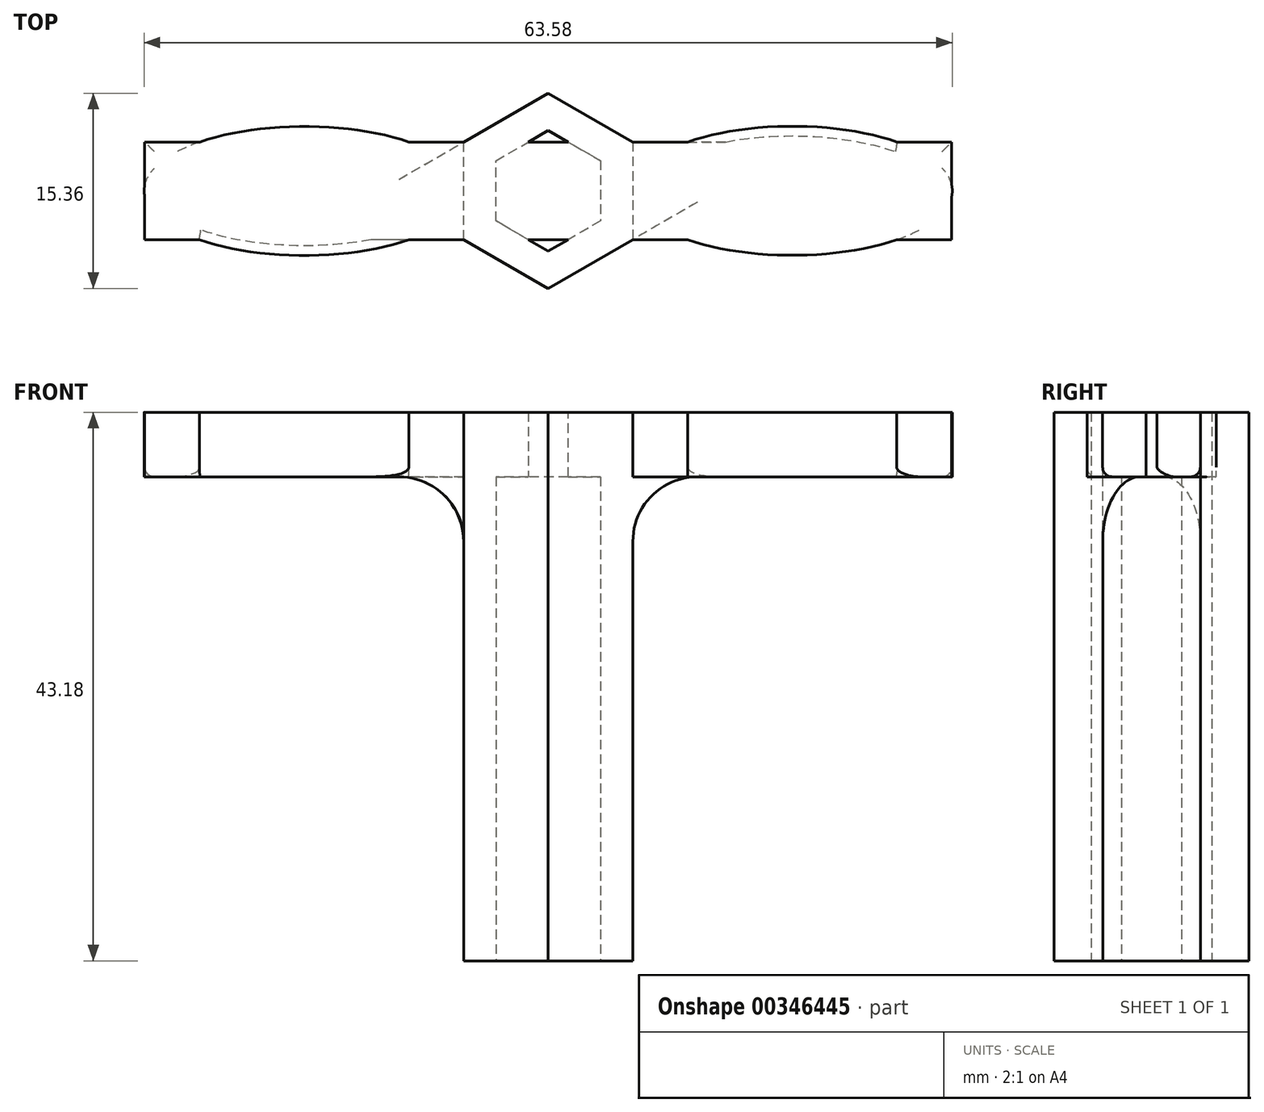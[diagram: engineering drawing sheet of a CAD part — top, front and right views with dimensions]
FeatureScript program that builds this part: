
annotation { "Feature Type Name" : "Feature", "Feature Type Description" : "" }
export const myFeature = defineFeature(function(context is Context, id is Id, definition is map)
    precondition{}
    {
        {
            var Q0;
            Q0=qCreatedBy(makeId("Top.planeOp"),FACE);
            var sketch = newSketch(context, id + "F0", { "sketchPlane" : qUnion([Q0])});
            skCircle(sketch, "E0.cCircle", {"center": v(0, 0) * mm, "radius": 4.11 * mm, "construction": true});
            skLineSegment(sketch, "E0.0", {"start": v(0, 4.75) * mm, "end": v(4.11, 2.38) * mm});
            skLineSegment(sketch, "E0.1", {"start": v(4.11, 2.38) * mm, "end": v(4.11, -2.37) * mm});
            skLineSegment(sketch, "E0.2", {"start": v(4.11, -2.37) * mm, "end": v(0, -4.75) * mm});
            skLineSegment(sketch, "E0.3", {"start": v(0, -4.75) * mm, "end": v(-4.11, -2.38) * mm});
            skLineSegment(sketch, "E0.4", {"start": v(-4.11, -2.38) * mm, "end": v(-4.11, 2.37) * mm});
            skLineSegment(sketch, "E0.5", {"start": v(-4.11, 2.37) * mm, "end": v(0, 4.75) * mm});
            skPoint(sketch, "E0.0.midPoint", {"position": v(2.06, 3.56) * mm});
            skCircle(sketch, "E1.cCircle", {"center": v(0, 0) * mm, "radius": 6.65 * mm, "construction": true});
            skLineSegment(sketch, "E1.0", {"start": v(0, 7.68) * mm, "end": v(6.65, 3.84) * mm});
            skLineSegment(sketch, "E1.1", {"start": v(6.65, 3.84) * mm, "end": v(6.65, -3.84) * mm});
            skLineSegment(sketch, "E1.2", {"start": v(6.65, -3.84) * mm, "end": v(0, -7.68) * mm});
            skLineSegment(sketch, "E1.3", {"start": v(0, -7.68) * mm, "end": v(-6.65, -3.84) * mm});
            skLineSegment(sketch, "E1.4", {"start": v(-6.65, -3.84) * mm, "end": v(-6.65, 3.84) * mm});
            skLineSegment(sketch, "E1.5", {"start": v(-6.65, 3.84) * mm, "end": v(0, 7.68) * mm});
            skPoint(sketch, "E1.0.midPoint", {"position": v(3.32, 5.76) * mm});
            skSolve(sketch);
        }
        {
            var Q0;
            Q0=qSketchRegion(id+"F0",true);
            extrude(context, id + "F1", {"entities" : qUnion([Q0]), "depth" : 43.18 * mm});
        }
        {
            var Q0;
            Q0=makeQuery(id+"F1.opExtrude","CAP_FACE",FACE,{"disambiguationData":[OSD([sQuery(id+"F0.wireOp",EDGE,"E0.0"),sQuery(id+"F0.wireOp",EDGE,"E0.1"),sQuery(id+"F0.wireOp",EDGE,"E0.2"),sQuery(id+"F0.wireOp",EDGE,"E0.3"),sQuery(id+"F0.wireOp",EDGE,"E0.4"),sQuery(id+"F0.wireOp",EDGE,"E0.5"),sQuery(id+"F0.wireOp",EDGE,"E1.0"),sQuery(id+"F0.wireOp",EDGE,"E1.1"),sQuery(id+"F0.wireOp",EDGE,"E1.2"),sQuery(id+"F0.wireOp",EDGE,"E1.3"),sQuery(id+"F0.wireOp",EDGE,"E1.4"),sQuery(id+"F0.wireOp",EDGE,"E1.5")])],"isStart":false});
            var sketch = newSketch(context, id + "F2", { "sketchPlane" : qUnion([Q0])});
            skLineSegment(sketch, "E2", {"start": v(0, 4.75) * mm, "end": v(0, -4.75) * mm});
            skLineSegment(sketch, "E3.bottom", {"start": v(31.75, 3.84) * mm, "end": v(-31.75, 3.84) * mm});
            skLineSegment(sketch, "E3.top", {"start": v(31.75, -3.84) * mm, "end": v(-31.75, -3.84) * mm});
            skLineSegment(sketch, "E3.left", {"start": v(31.75, 3.84) * mm, "end": v(31.75, -3.84) * mm});
            skLineSegment(sketch, "E3.right", {"start": v(-31.75, 3.84) * mm, "end": v(-31.75, -3.84) * mm});
            skPoint(sketch, "E3.middle", {"position": v(0, 0) * mm});
            skLineSegment(sketch, "E4", {"start": v(-6.65, 0) * mm, "end": v(-31.75, -0.01) * mm});
            skEllipse(sketch, "E5", {"center": v(-19.2, 0) * mm, "majorRadius": 12.6 * mm, "minorRadius": 5.08 * mm, "majorAxis": v(-1, 0)});
            skLineSegment(sketch, "E6", {"start": v(6.65, 0) * mm, "end": v(31.75, 0) * mm});
            skEllipse(sketch, "E7", {"center": v(19.2, 0) * mm, "majorRadius": 12.6 * mm, "minorRadius": 5.08 * mm, "majorAxis": v(1, 0)});
            skSolve(sketch);
        }
        {
            var Q0;
            Q0 = qSketchRegion(id + "F2", true);
            extrude(context, id + "F3", {"entities" : qUnion([Q0]), "operationType" : NewBodyOperationType.ADD, "oppositeDirection" : true, "depth" : 5.08 * mm});
        }
        {
            var Q0;
            {var subQ0=sQuery(id+"F2.wireOp",EDGE,"E5");var subQ1=sQuery(id+"F2.wireOp",EDGE,"E3.bottom");Q0=makeQuery(id+"F3.opExtrude","CAP_EDGE",EDGE,{"disambiguationData":[OSD([subQ0]),TDD([makeQuery(id+"F2.imprint","IMPRINT",EDGE,{"disambiguationData":[TD([[makeQuery(id+"F2.imprint","INTERSECT",VERTEX,{"disambiguationData":[OD(0.0)],"derivedFrom":[subQ1,subQ0]}),-1.0]])],"derivedFrom":subQ0})])],"isStart":false});}
            var Q1;
            {var subQ0=sQuery(id+"F2.wireOp",EDGE,"E3.bottom");Q1=makeQuery(id+"F3.opExtrude","CAP_EDGE",EDGE,{"disambiguationData":[OSD([subQ0]),TDD([makeQuery(id+"F2.imprint","IMPRINT",EDGE,{"disambiguationData":[TD([[makeQuery(id+"F2.imprint","INTERSECT",VERTEX,{"derivedFrom":[subQ0,sQuery(id+"F2.wireOp",EDGE,"E3.right")]}),1.0]])],"derivedFrom":subQ0})])],"isStart":false});}
            var Q2;
            {var subQ0=sQuery(id+"F2.wireOp",EDGE,"E3.top");Q2=makeQuery(id+"F3.opExtrude","CAP_EDGE",EDGE,{"disambiguationData":[OSD([subQ0]),TDD([makeQuery(id+"F2.imprint","IMPRINT",EDGE,{"disambiguationData":[TD([[makeQuery(id+"F2.imprint","INTERSECT",VERTEX,{"derivedFrom":[subQ0,sQuery(id+"F2.wireOp",EDGE,"E3.right")]}),1.0]])],"derivedFrom":subQ0})])],"isStart":false});}
            var Q3;
            {var subQ0=sQuery(id+"F2.wireOp",EDGE,"E5");var subQ1=sQuery(id+"F2.wireOp",EDGE,"E3.top");Q3=makeQuery(id+"F3.opExtrude","CAP_EDGE",EDGE,{"disambiguationData":[OSD([subQ0]),TDD([makeQuery(id+"F2.imprint","IMPRINT",EDGE,{"disambiguationData":[TD([[makeQuery(id+"F2.imprint","INTERSECT",VERTEX,{"disambiguationData":[OD(0.0)],"derivedFrom":[subQ1,subQ0]}),1.0]])],"derivedFrom":subQ0})])],"isStart":false});}
            var Q4;
            {var subQ0=sQuery(id+"F2.wireOp",EDGE,"E3.right");Q4=makeQuery(id+"F3.opExtrude","CAP_EDGE",EDGE,{"disambiguationData":[OSD([subQ0]),TDD([makeQuery(id+"F2.imprint","IMPRINT",EDGE,{"disambiguationData":[TD([[makeQuery(id+"F2.imprint","INTERSECT",VERTEX,{"derivedFrom":[sQuery(id+"F2.wireOp",EDGE,"E3.bottom"),subQ0]}),-1.0]])],"derivedFrom":subQ0})])],"isStart":false});}
            var Q5;
            {var subQ0=sQuery(id+"F2.wireOp",EDGE,"E3.left");Q5=makeQuery(id+"F3.opExtrude","CAP_EDGE",EDGE,{"disambiguationData":[OSD([subQ0]),TDD([makeQuery(id+"F2.imprint","IMPRINT",EDGE,{"disambiguationData":[TD([[makeQuery(id+"F2.imprint","INTERSECT",VERTEX,{"derivedFrom":[sQuery(id+"F2.wireOp",EDGE,"E3.bottom"),subQ0]}),-1.0]])],"derivedFrom":subQ0})])],"isStart":false});}
            var Q6;
            {var subQ0=sQuery(id+"F2.wireOp",EDGE,"E3.top");Q6=makeQuery(id+"F3.opExtrude","CAP_EDGE",EDGE,{"disambiguationData":[OSD([subQ0]),TDD([makeQuery(id+"F2.imprint","IMPRINT",EDGE,{"disambiguationData":[TD([[makeQuery(id+"F2.imprint","INTERSECT",VERTEX,{"derivedFrom":[subQ0,sQuery(id+"F2.wireOp",EDGE,"E3.left")]}),-1.0]])],"derivedFrom":subQ0})])],"isStart":false});}
            var Q7;
            {var subQ0=sQuery(id+"F2.wireOp",EDGE,"E7");var subQ1=sQuery(id+"F2.wireOp",EDGE,"E3.top");Q7=makeQuery(id+"F3.opExtrude","CAP_EDGE",EDGE,{"disambiguationData":[OSD([subQ0]),TDD([makeQuery(id+"F2.imprint","IMPRINT",EDGE,{"disambiguationData":[TD([[makeQuery(id+"F2.imprint","INTERSECT",VERTEX,{"disambiguationData":[OD(0.0)],"derivedFrom":[subQ1,subQ0]}),1.0]])],"derivedFrom":subQ0})])],"isStart":false});}
            var Q8;
            {var subQ0=sQuery(id+"F2.wireOp",EDGE,"E7");var subQ1=sQuery(id+"F2.wireOp",EDGE,"E3.bottom");Q8=makeQuery(id+"F3.opExtrude","CAP_EDGE",EDGE,{"disambiguationData":[OSD([subQ0]),TDD([makeQuery(id+"F2.imprint","IMPRINT",EDGE,{"disambiguationData":[TD([[makeQuery(id+"F2.imprint","INTERSECT",VERTEX,{"disambiguationData":[OD(0.0)],"derivedFrom":[subQ1,subQ0]}),-1.0]])],"derivedFrom":subQ0})])],"isStart":false});}
            var Q9;
            {var subQ0=sQuery(id+"F2.wireOp",EDGE,"E3.bottom");Q9=makeQuery(id+"F3.opExtrude","CAP_EDGE",EDGE,{"disambiguationData":[OSD([subQ0]),TDD([makeQuery(id+"F2.imprint","IMPRINT",EDGE,{"disambiguationData":[TD([[makeQuery(id+"F2.imprint","INTERSECT",VERTEX,{"derivedFrom":[subQ0,sQuery(id+"F2.wireOp",EDGE,"E3.left")]}),-1.0]])],"derivedFrom":subQ0})])],"isStart":false});}
            fillet(context, id + "F4", {"entities" : qUnion([Q0, Q1, Q2, Q3, Q4, Q5, Q6, Q7, Q8, Q9]), "radius" : 0.76 * mm, "tangentPropagation" : true, "allowEdgeOverflow" : false});
        }
        {
            var Q0;
            Q0=makeQuery(id+"F3.boolean.opBoolean","INTERSECT",EDGE,{"derivedFrom":[makeQuery(id+"F1.opExtrude","SWEPT_FACE",FACE,{"disambiguationData":[OSD([sQuery(id+"F0.wireOp",EDGE,"E1.1")])]}),makeQuery(id+"F3.opExtrude","CAP_FACE",FACE,{"disambiguationData":[OSD([sQuery(id+"F2.wireOp",EDGE,"E3.bottom"),sQuery(id+"F2.wireOp",EDGE,"E3.top"),sQuery(id+"F2.wireOp",EDGE,"E3.left"),sQuery(id+"F2.wireOp",EDGE,"E3.right"),sQuery(id+"F2.wireOp",EDGE,"E5"),sQuery(id+"F2.wireOp",EDGE,"E7")])],"isStart":false})]});
            var Q1;
            Q1=makeQuery(id+"F3.boolean.opBoolean","INTERSECT",EDGE,{"derivedFrom":[makeQuery(id+"F1.opExtrude","SWEPT_FACE",FACE,{"disambiguationData":[OSD([sQuery(id+"F0.wireOp",EDGE,"E1.4")])]}),makeQuery(id+"F3.opExtrude","CAP_FACE",FACE,{"disambiguationData":[OSD([sQuery(id+"F2.wireOp",EDGE,"E3.bottom"),sQuery(id+"F2.wireOp",EDGE,"E3.top"),sQuery(id+"F2.wireOp",EDGE,"E3.left"),sQuery(id+"F2.wireOp",EDGE,"E3.right"),sQuery(id+"F2.wireOp",EDGE,"E5"),sQuery(id+"F2.wireOp",EDGE,"E7")])],"isStart":false})]});
            fillet(context, id + "F5", {"entities" : qUnion([Q0, Q1]), "radius" : 5.08 * mm, "tangentPropagation" : true, "allowEdgeOverflow" : false});
        }
    });
